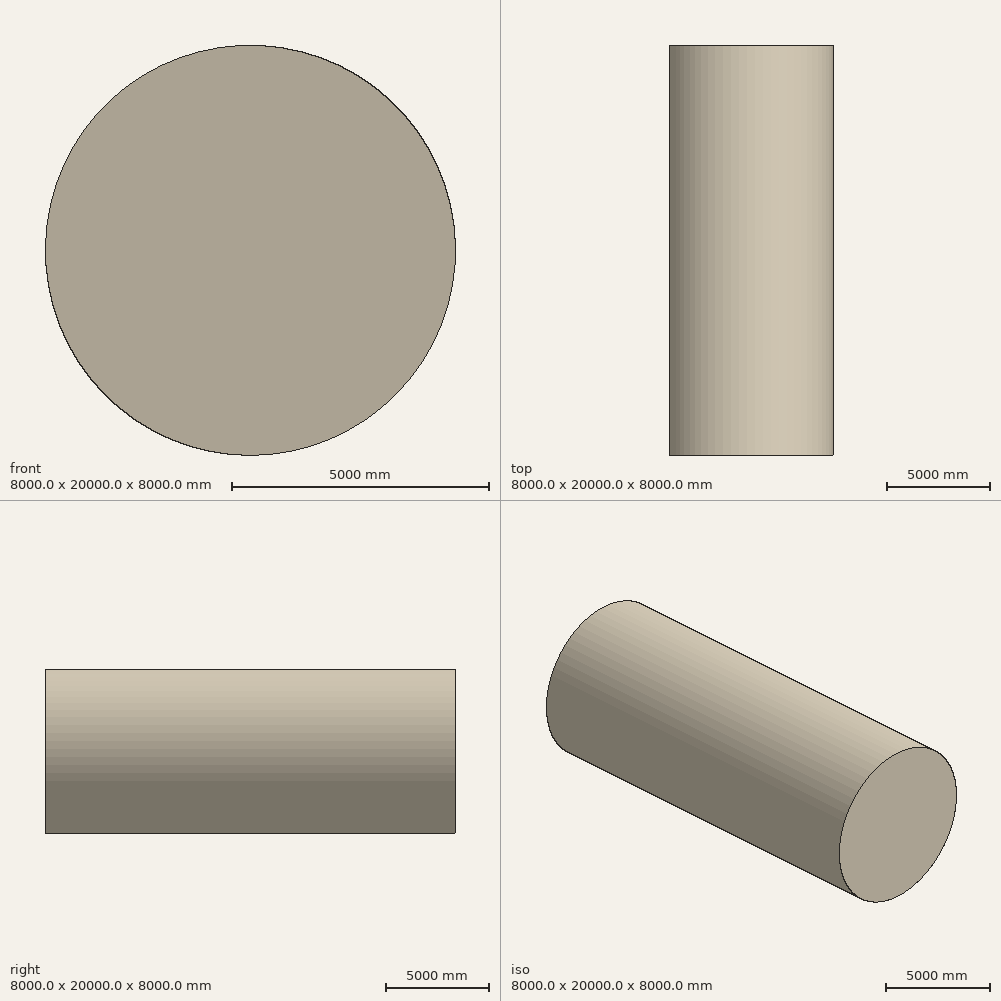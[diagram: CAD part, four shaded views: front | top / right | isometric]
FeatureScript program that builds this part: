
annotation { "Feature Type Name" : "Feature", "Feature Type Description" : "" }
export const myFeature = defineFeature(function(context is Context, id is Id, definition is map)
    precondition{}
    {
        {
            var Q0;
            Q0=qCreatedBy(makeId("Front.planeOp"),FACE);
            var sketch = newSketch(context, id + "F0", { "sketchPlane" : qUnion([Q0])});
            skCircle(sketch, "E0", {"center": v(0, 0) * mm, "radius": 4000 * mm});
            skSolve(sketch);
        }
        {
            var Q0;
            Q0=makeQuery(id+"F0.imprint","IMPRINT",FACE,{"disambiguationData":[TD([[makeQuery(id+"F0.imprint","IMPRINT",EDGE,{"derivedFrom":sQuery(id+"F0.wireOp",EDGE,"E0")}),1.0]])]});
            extrude(context, id + "F1", {"entities" : qUnion([Q0]), "depth" : 20000 * mm});
        }
    });
